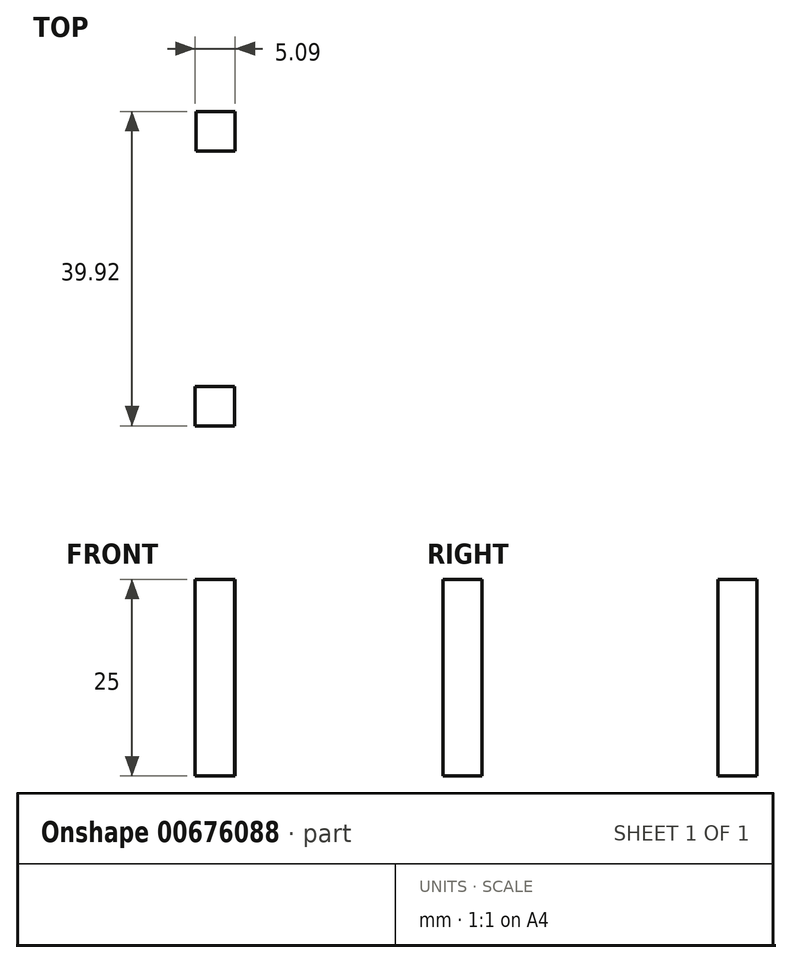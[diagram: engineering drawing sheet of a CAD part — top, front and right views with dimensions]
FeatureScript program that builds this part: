
annotation { "Feature Type Name" : "Feature", "Feature Type Description" : "" }
export const myFeature = defineFeature(function(context is Context, id is Id, definition is map)
    precondition{}
    {
        {
            var Q0;
            Q0=qCreatedBy(makeId("Top.planeOp"),FACE);
            var sketch = newSketch(context, id + "F0", { "sketchPlane" : qUnion([Q0])});
            skLineSegment(sketch, "E0.bottom", {"start": v(-5, 17.5) * mm, "end": v(5, 17.5) * mm});
            skLineSegment(sketch, "E0.top", {"start": v(-5, -17.5) * mm, "end": v(5, -17.5) * mm});
            skLineSegment(sketch, "E0.left", {"start": v(-5, 17.5) * mm, "end": v(-5, -17.5) * mm});
            skLineSegment(sketch, "E0.right", {"start": v(5, 17.5) * mm, "end": v(5, -17.5) * mm});
            skPoint(sketch, "E0.middle", {"position": v(0, 0) * mm});
            skPoint(sketch, "E1.middle", {"position": v(-5, 17.5) * mm});
            skLineSegment(sketch, "E2.bottom", {"start": v(-2.5, 20) * mm, "end": v(2.5, 20) * mm});
            skLineSegment(sketch, "E2.top", {"start": v(-2.5, 15) * mm, "end": v(2.5, 15) * mm});
            skLineSegment(sketch, "E2.left", {"start": v(-2.5, 20) * mm, "end": v(-2.5, 15) * mm});
            skLineSegment(sketch, "E2.right", {"start": v(2.5, 20) * mm, "end": v(2.5, 15) * mm});
            skPoint(sketch, "E2.middle", {"position": v(0, 17.5) * mm});
            skLineSegment(sketch, "E3.bottom", {"start": v(-2.6, -14.92) * mm, "end": v(2.4, -14.92) * mm});
            skLineSegment(sketch, "E3.top", {"start": v(-2.6, -19.92) * mm, "end": v(2.4, -19.92) * mm});
            skLineSegment(sketch, "E3.left", {"start": v(-2.6, -14.92) * mm, "end": v(-2.6, -19.92) * mm});
            skLineSegment(sketch, "E3.right", {"start": v(2.4, -14.92) * mm, "end": v(2.4, -19.92) * mm});
            skSolve(sketch);
        }
        {
            var Q0;
            {var subQ5=sQuery(id+"F0.wireOp",EDGE,"E3.top");Q0=makeQuery(id+"F0.imprint","IMPRINT",FACE,{"disambiguationData":[TD([[makeQuery(id+"F0.imprint","IMPRINT",EDGE,{"derivedFrom":subQ5}),1.0]])]});}
            var Q1;
            {var subQ5=sQuery(id+"F0.wireOp",EDGE,"E3.bottom");Q1=makeQuery(id+"F0.imprint","IMPRINT",FACE,{"disambiguationData":[TD([[makeQuery(id+"F0.imprint","IMPRINT",EDGE,{"derivedFrom":subQ5}),-1.0]])]});}
            var Q2;
            {var subQ5=sQuery(id+"F0.wireOp",EDGE,"E2.bottom");Q2=makeQuery(id+"F0.imprint","IMPRINT",FACE,{"disambiguationData":[TD([[makeQuery(id+"F0.imprint","IMPRINT",EDGE,{"derivedFrom":subQ5}),-1.0]])]});}
            var Q3;
            {var subQ5=sQuery(id+"F0.wireOp",EDGE,"E2.top");Q3=makeQuery(id+"F0.imprint","IMPRINT",FACE,{"disambiguationData":[TD([[makeQuery(id+"F0.imprint","IMPRINT",EDGE,{"derivedFrom":subQ5}),1.0]])]});}
            extrude(context, id + "F1", {"entities" : qUnion([Q0, Q1, Q2, Q3]), "oppositeDirection" : true, "depth" : 25 * mm, "offsetDistance" : 25.4 * mm});
        }
    });
